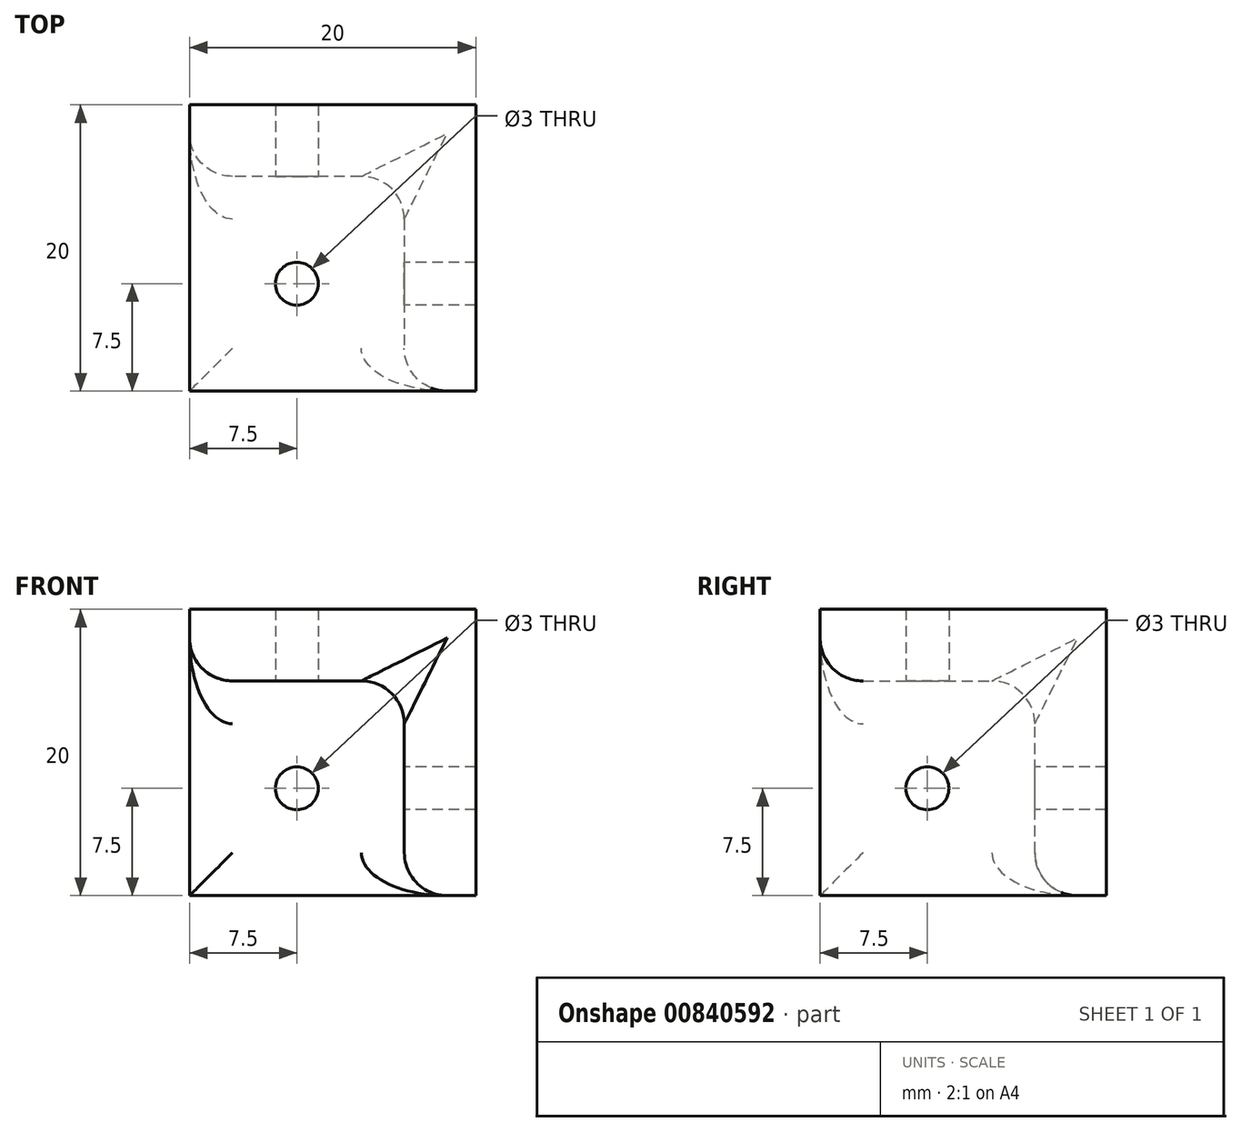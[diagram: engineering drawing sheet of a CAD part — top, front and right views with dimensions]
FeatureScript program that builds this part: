
annotation { "Feature Type Name" : "Feature", "Feature Type Description" : "" }
export const myFeature = defineFeature(function(context is Context, id is Id, definition is map)
    precondition{}
    {
        {
            var Q0;
            Q0=qCreatedBy(makeId("Front.planeOp"),FACE);
            var sketch = newSketch(context, id + "F0", { "sketchPlane" : qUnion([Q0])});
            skLineSegment(sketch, "E0.bottom", {"start": v(0, 0) * mm, "end": v(20, 0) * mm});
            skLineSegment(sketch, "E0.top", {"start": v(0, -20) * mm, "end": v(20, -20) * mm});
            skLineSegment(sketch, "E0.left", {"start": v(0, 0) * mm, "end": v(0, -20) * mm});
            skLineSegment(sketch, "E0.right", {"start": v(20, 0) * mm, "end": v(20, -20) * mm});
            skSolve(sketch);
        }
        {
            var Q0;
            Q0=makeQuery(id+"F0.imprint","IMPRINT",FACE,{"disambiguationData":[TD([[makeQuery(id+"F0.imprint","IMPRINT",EDGE,{"derivedFrom":sQuery(id+"F0.wireOp",EDGE,"E0.bottom")}),-1.0]])]});
            extrude(context, id + "F1", {"entities" : qUnion([Q0]), "depth" : 5 * mm, "offsetDistance" : 25 * mm});
        }
        {
            var Q0;
            Q0=makeQuery(id+"F1.opExtrude","SWEPT_FACE",FACE,{"disambiguationData":[OSD([sQuery(id+"F0.wireOp",EDGE,"E0.right")])]});
            var sketch = newSketch(context, id + "F2", { "sketchPlane" : qUnion([Q0])});
            skLineSegment(sketch, "E1.bottom", {"start": v(0, 0) * mm, "end": v(-20, 0) * mm});
            skLineSegment(sketch, "E1.top", {"start": v(0, -20) * mm, "end": v(-20, -20) * mm});
            skLineSegment(sketch, "E1.left", {"start": v(0, 0) * mm, "end": v(0, -20) * mm});
            skLineSegment(sketch, "E1.right", {"start": v(-20, 0) * mm, "end": v(-20, -20) * mm});
            skSolve(sketch);
        }
        {
            var Q0;
            Q0 = qSketchRegion(id + "F2", true);
            extrude(context, id + "F3", {"entities" : qUnion([Q0]), "operationType" : NewBodyOperationType.ADD, "oppositeDirection" : true, "depth" : 5 * mm, "offsetDistance" : 25 * mm});
        }
        {
            var Q0;
            Q0=makeQuery(id+"F3.boolean.opBoolean","MERGE",FACE,{"derivedFrom":[makeQuery(id+"F1.opExtrude","SWEPT_FACE",FACE,{"disambiguationData":[OSD([sQuery(id+"F0.wireOp",EDGE,"E0.bottom")])]}),makeQuery(id+"F3.opExtrude","SWEPT_FACE",FACE,{"disambiguationData":[OSD([sQuery(id+"F2.wireOp",EDGE,"E1.bottom")])]})]});
            var sketch = newSketch(context, id + "F4", { "sketchPlane" : qUnion([Q0])});
            skLineSegment(sketch, "E2.bottom", {"start": v(0, 0) * mm, "end": v(20, 0) * mm});
            skLineSegment(sketch, "E2.top", {"start": v(0, -20) * mm, "end": v(20, -20) * mm});
            skLineSegment(sketch, "E2.left", {"start": v(0, 0) * mm, "end": v(0, -20) * mm});
            skLineSegment(sketch, "E2.right", {"start": v(20, 0) * mm, "end": v(20, -20) * mm});
            skSolve(sketch);
        }
        {
            var Q0;
            {var subQ1=sQuery(id+"F4.wireOp",EDGE,"E2.bottom");Q0=makeQuery(id+"F4.imprint","IMPRINT",FACE,{"disambiguationData":[TD([[makeQuery(id+"F4.imprint","IMPRINT",EDGE,{"derivedFrom":subQ1}),-1.0]])]});}
            var Q1;
            {var subQ4=makeQuery(id+"F1.opExtrude","CAP_EDGE",EDGE,{"disambiguationData":[OSD([sQuery(id+"F0.wireOp",EDGE,"E0.bottom")])],"isStart":false});Q1=makeQuery(id+"F4.imprint","IMPRINT",FACE,{"disambiguationData":[TD([[makeQuery(id+"F4.imprint","IMPRINT",EDGE,{"derivedFrom":subQ4}),-1.0]])]});}
            extrude(context, id + "F5", {"entities" : qUnion([Q0, Q1]), "operationType" : NewBodyOperationType.ADD, "oppositeDirection" : true, "depth" : 5 * mm, "offsetDistance" : 25 * mm});
        }
        {
            var Q0;
            Q0=makeQuery(id+"F5.opExtrude","CAP_FACE",FACE,{"disambiguationData":[OSD([sQuery(id+"F4.wireOp",EDGE,"E2.bottom"),sQuery(id+"F4.wireOp",EDGE,"E2.top"),sQuery(id+"F4.wireOp",EDGE,"E2.left"),sQuery(id+"F4.wireOp",EDGE,"E2.right")])],"isStart":false});
            var sketch = newSketch(context, id + "F6", { "sketchPlane" : qUnion([Q0])});
            skLineSegment(sketch, "E3", {"start": v(7.5, 20) * mm, "end": v(7.5, 5) * mm, "construction": true});
            skLineSegment(sketch, "E4", {"start": v(7.5, 5) * mm, "end": v(15, 12.5) * mm, "construction": true});
            skLineSegment(sketch, "E5", {"start": v(15, 12.5) * mm, "end": v(0, 12.5) * mm, "construction": true});
            skCircle(sketch, "E6", {"center": v(7.5, 12.5) * mm, "radius": 1.5 * mm, "construction": true});
            skCircle(sketch, "E7", {"center": v(7.5, 12.5) * mm, "radius": 1.5 * mm});
            skSolve(sketch);
        }
        {
            var Q0;
            Q0 = qSketchRegion(id + "F6", true);
            extrude(context, id + "F7", {"entities" : qUnion([Q0]), "operationType" : NewBodyOperationType.REMOVE, "oppositeDirection" : true, "depth" : 6 * mm, "offsetDistance" : 25 * mm});
        }
        {
            var Q0;
            Q0=makeQuery(id+"F3.opExtrude","CAP_FACE",FACE,{"disambiguationData":[OSD([sQuery(id+"F2.wireOp",EDGE,"E1.bottom"),sQuery(id+"F2.wireOp",EDGE,"E1.top"),sQuery(id+"F2.wireOp",EDGE,"E1.left"),sQuery(id+"F2.wireOp",EDGE,"E1.right")])],"isStart":false});
            var sketch = newSketch(context, id + "F8", { "sketchPlane" : qUnion([Q0])});
            skLineSegment(sketch, "E8", {"start": v(12.5, -5) * mm, "end": v(12.5, -20) * mm, "construction": true});
            skLineSegment(sketch, "E9", {"start": v(12.5, -20) * mm, "end": v(20, -12.5) * mm, "construction": true});
            skLineSegment(sketch, "E10", {"start": v(20, -12.5) * mm, "end": v(5, -12.5) * mm, "construction": true});
            skCircle(sketch, "E11", {"center": v(12.5, -12.5) * mm, "radius": 1.5 * mm});
            skSolve(sketch);
        }
        {
            var Q0;
            Q0 = qSketchRegion(id + "F8", true);
            extrude(context, id + "F9", {"entities" : qUnion([Q0]), "operationType" : NewBodyOperationType.REMOVE, "oppositeDirection" : true, "depth" : 25 * mm, "offsetDistance" : 25 * mm});
        }
        {
            var Q0;
            Q0=makeQuery(id+"F1.opExtrude","CAP_FACE",FACE,{"disambiguationData":[OSD([sQuery(id+"F0.wireOp",EDGE,"E0.bottom"),sQuery(id+"F0.wireOp",EDGE,"E0.top"),sQuery(id+"F0.wireOp",EDGE,"E0.left"),sQuery(id+"F0.wireOp",EDGE,"E0.right")])],"isStart":false});
            var sketch = newSketch(context, id + "F10", { "sketchPlane" : qUnion([Q0])});
            skLineSegment(sketch, "E12", {"start": v(7.5, -5) * mm, "end": v(7.5, -20) * mm, "construction": true});
            skLineSegment(sketch, "E13", {"start": v(7.5, -20) * mm, "end": v(0, -12.5) * mm, "construction": true});
            skLineSegment(sketch, "E14", {"start": v(0, -12.5) * mm, "end": v(15, -12.5) * mm, "construction": true});
            skCircle(sketch, "E15", {"center": v(7.5, -12.5) * mm, "radius": 1.5 * mm});
            skSolve(sketch);
        }
        {
            var Q0;
            Q0 = qSketchRegion(id + "F10", true);
            extrude(context, id + "F11", {"entities" : qUnion([Q0]), "operationType" : NewBodyOperationType.REMOVE, "oppositeDirection" : true, "depth" : 25 * mm, "offsetDistance" : 25 * mm});
        }
        {
            var Q0;
            Q0=makeQuery(id+"F1.opExtrude","CAP_EDGE",EDGE,{"disambiguationData":[OSD([sQuery(id+"F0.wireOp",EDGE,"E0.left")])],"isStart":false});
            var Q1;
            Q1=makeQuery(id+"F5.opExtrude","CAP_EDGE",EDGE,{"disambiguationData":[OSD([sQuery(id+"F4.wireOp",EDGE,"E2.left")])],"isStart":false});
            var Q2;
            Q2=makeQuery(id+"F5.opExtrude","CAP_EDGE",EDGE,{"disambiguationData":[OSD([sQuery(id+"F4.wireOp",EDGE,"E2.top")])],"isStart":false});
            var Q3;
            Q3=makeQuery(id+"F3.opExtrude","CAP_EDGE",EDGE,{"disambiguationData":[OSD([sQuery(id+"F2.wireOp",EDGE,"E1.right")])],"isStart":false});
            var Q4;
            Q4=makeQuery(id+"F3.opExtrude","CAP_EDGE",EDGE,{"disambiguationData":[OSD([sQuery(id+"F2.wireOp",EDGE,"E1.top")])],"isStart":false});
            var Q5;
            Q5=makeQuery(id+"F1.opExtrude","CAP_EDGE",EDGE,{"disambiguationData":[OSD([sQuery(id+"F0.wireOp",EDGE,"E0.top")])],"isStart":false});
            fillet(context, id + "F12", {"entities" : qUnion([Q0, Q1, Q2, Q3, Q4, Q5]), "radius" : 3 * mm, "tangentPropagation" : true, "allowEdgeOverflow" : false});
        }
        {
            var Q0;
            Q0=makeQuery(id+"F5.boolean.opBoolean","INTERSECT",EDGE,{"derivedFrom":[makeQuery(id+"F3.opExtrude","CAP_FACE",FACE,{"disambiguationData":[OSD([sQuery(id+"F2.wireOp",EDGE,"E1.bottom"),sQuery(id+"F2.wireOp",EDGE,"E1.top"),sQuery(id+"F2.wireOp",EDGE,"E1.left"),sQuery(id+"F2.wireOp",EDGE,"E1.right")])],"isStart":false}),makeQuery(id+"F5.opExtrude","CAP_FACE",FACE,{"disambiguationData":[OSD([sQuery(id+"F4.wireOp",EDGE,"E2.bottom"),sQuery(id+"F4.wireOp",EDGE,"E2.top"),sQuery(id+"F4.wireOp",EDGE,"E2.left"),sQuery(id+"F4.wireOp",EDGE,"E2.right")])],"isStart":false})]});
            var Q1;
            Q1=makeQuery(id+"F3.boolean.opBoolean","INTERSECT",EDGE,{"derivedFrom":[makeQuery(id+"F1.opExtrude","CAP_FACE",FACE,{"disambiguationData":[OSD([sQuery(id+"F0.wireOp",EDGE,"E0.bottom"),sQuery(id+"F0.wireOp",EDGE,"E0.top"),sQuery(id+"F0.wireOp",EDGE,"E0.left"),sQuery(id+"F0.wireOp",EDGE,"E0.right")])],"isStart":false}),makeQuery(id+"F3.opExtrude","CAP_FACE",FACE,{"disambiguationData":[OSD([sQuery(id+"F2.wireOp",EDGE,"E1.bottom"),sQuery(id+"F2.wireOp",EDGE,"E1.top"),sQuery(id+"F2.wireOp",EDGE,"E1.left"),sQuery(id+"F2.wireOp",EDGE,"E1.right")])],"isStart":false})]});
            var Q2;
            Q2=makeQuery(id+"F5.boolean.opBoolean","INTERSECT",EDGE,{"derivedFrom":[makeQuery(id+"F1.opExtrude","CAP_FACE",FACE,{"disambiguationData":[OSD([sQuery(id+"F0.wireOp",EDGE,"E0.bottom"),sQuery(id+"F0.wireOp",EDGE,"E0.top"),sQuery(id+"F0.wireOp",EDGE,"E0.left"),sQuery(id+"F0.wireOp",EDGE,"E0.right")])],"isStart":false}),makeQuery(id+"F5.opExtrude","CAP_FACE",FACE,{"disambiguationData":[OSD([sQuery(id+"F4.wireOp",EDGE,"E2.bottom"),sQuery(id+"F4.wireOp",EDGE,"E2.top"),sQuery(id+"F4.wireOp",EDGE,"E2.left"),sQuery(id+"F4.wireOp",EDGE,"E2.right")])],"isStart":false})]});
            fillet(context, id + "F13", {"entities" : qUnion([Q0, Q1, Q2]), "radius" : 3 * mm, "tangentPropagation" : true, "allowEdgeOverflow" : false});
        }
    });
